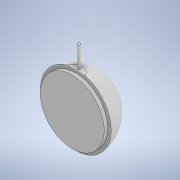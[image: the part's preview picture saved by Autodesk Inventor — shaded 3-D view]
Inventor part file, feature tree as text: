
AUTODESK INVENTOR PART (.ipt)
format: ipt  version: 2022 (Build 260153000, 153)  size: 142,336 bytes
history: native  units: in
note: dims shown in document units (in); Inventor stores cm internally (conversion verified against a paired STEP export)
features: sketch x5, extrude x4, revolve x1
ambient origin geometry x8: Origin, YZ Plane, XZ Plane, XY Plane, X Axis, Y Axis, Z Axis, Center Point
bodies: Body1 (feature_tree)
feature tree (10):
  revolve  "Revolution2"  [1 undecoded]
  extrude  "Extrusion5"  Depth=1.25in TaperAngle=0.0deg
  extrude  "Extrusion6"  Depth=0.1125in
  extrude  "Extrusion7"  Depth=0.75in TaperAngle=0.0deg
  extrude  "Extrusion8"  Depth=0.0344in
  sketch  "Sketch6"  dims[d19=180.0deg d20=0.125in d21=0.0in]
  sketch  "Sketch9"  dims[d23=0.125in d24=0.0in d25=1.2in d26=1.25in d27=0.0in d28=0.0in]
  sketch  "Sketch10"  dims[d29=0.225in d30=0.1125in]
  sketch  "Sketch11"  dims[d31=0.1in d32=0.75in d33=0.0in]
  sketch  "Sketch12"  dims[d10=0.5in d11=0.0344in d12=0.5in d13=0.0344in]
note: 1 required parameter value undecoded (feature->parameter linkage not recoverable at this tier; creation-order binding heuristic only, values carry confidence <= 0.55)
